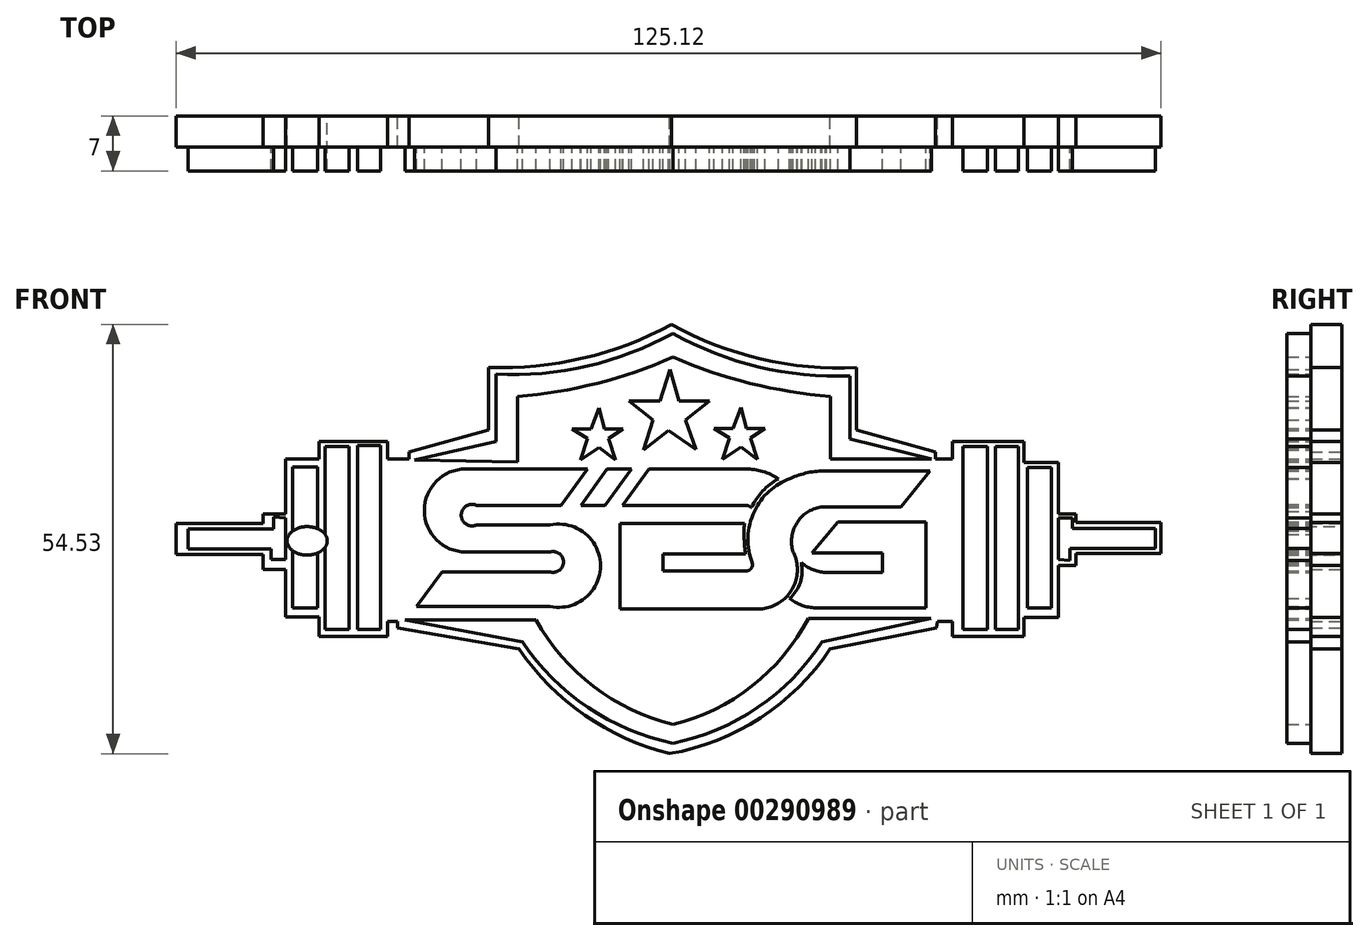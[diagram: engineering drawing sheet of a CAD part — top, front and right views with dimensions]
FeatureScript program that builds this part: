
annotation { "Feature Type Name" : "Feature", "Feature Type Description" : "" }
export const myFeature = defineFeature(function(context is Context, id is Id, definition is map)
    precondition{}
    {
        {
            var Q0;
            Q0=qCreatedBy(makeId("Front.planeOp"),FACE);
            var sketch = newSketch(context, id + "F0", { "sketchPlane" : qUnion([Q0])});
            skLineSegment(sketch, "E0", {"start": v(-28.73, 27.46) * mm, "end": v(-18.36, 29.84) * mm});
            skLineSegment(sketch, "E1", {"start": v(-18.36, 29.84) * mm, "end": v(-18.36, 38.37) * mm});
            skLineSegment(sketch, "E2", {"start": v(26.58, 38.16) * mm, "end": v(26.58, 30.16) * mm});
            skLineSegment(sketch, "E3", {"start": v(26.58, 30.16) * mm, "end": v(36.96, 27.57) * mm});
            skLineSegment(sketch, "E4", {"start": v(36.96, 27.57) * mm, "end": v(24.1, 27.57) * mm});
            skLineSegment(sketch, "E5", {"start": v(24.1, 27.57) * mm, "end": v(24.1, 35.56) * mm});
            skLineSegment(sketch, "E6", {"start": v(-15.66, 35.56) * mm, "end": v(-15.66, 27.24) * mm});
            skLineSegment(sketch, "E7", {"start": v(-15.66, 27.24) * mm, "end": v(-28.73, 27.46) * mm});
            skArc(sketch, "E8", {"start": v(-18.36, 38.37) * mm, "mid": v(-6.76, 39.4) * mm, "end": v(4.11, 43.56) * mm});
            skArc(sketch, "E9", {"start": v(4.11, 43.56) * mm, "mid": v(14.97, 39.29) * mm, "end": v(26.58, 38.16) * mm});
            skArc(sketch, "E10", {"start": v(-15.66, 35.56) * mm, "mid": v(-5.56, 37.2) * mm, "end": v(4.11, 40.53) * mm});
            skArc(sketch, "E11", {"start": v(4.11, 40.53) * mm, "mid": v(13.9, 37.21) * mm, "end": v(24.1, 35.56) * mm});
            skLineSegment(sketch, "E12", {"start": v(-29.92, 7.15) * mm, "end": v(-13.28, 7.15) * mm});
            skLineSegment(sketch, "E13", {"start": v(21.29, 7.37) * mm, "end": v(36.85, 7.37) * mm});
            skLineSegment(sketch, "E14", {"start": v(36.85, 7.37) * mm, "end": v(23.02, 4.34) * mm});
            skLineSegment(sketch, "E15", {"start": v(-15.01, 4.34) * mm, "end": v(-29.92, 7.15) * mm});
            skArc(sketch, "E16", {"start": v(-13.28, 7.15) * mm, "mid": v(-5.98, -1.32) * mm, "end": v(4.11, -6.14) * mm});
            skArc(sketch, "E17", {"start": v(4.11, -6.14) * mm, "mid": v(14.17, -1.26) * mm, "end": v(21.29, 7.37) * mm});
            skArc(sketch, "E18", {"start": v(4.11, -8.52) * mm, "mid": v(14.86, -4) * mm, "end": v(23.02, 4.34) * mm});
            skArc(sketch, "E19", {"start": v(-15.01, 4.34) * mm, "mid": v(-6.71, -3.97) * mm, "end": v(4.11, -8.52) * mm});
            skLineSegment(sketch, "E20.bottom", {"start": v(-35.97, 29.3) * mm, "end": v(-33.05, 29.3) * mm});
            skLineSegment(sketch, "E20.top", {"start": v(-35.97, 5.96) * mm, "end": v(-33.05, 5.96) * mm});
            skLineSegment(sketch, "E20.left", {"start": v(-35.97, 29.3) * mm, "end": v(-35.97, 5.96) * mm});
            skLineSegment(sketch, "E20.right", {"start": v(-33.05, 29.3) * mm, "end": v(-33.05, 5.96) * mm});
            skLineSegment(sketch, "E21.bottom", {"start": v(-40.08, 29.19) * mm, "end": v(-37.05, 29.19) * mm});
            skLineSegment(sketch, "E21.top", {"start": v(-40.08, 5.96) * mm, "end": v(-37.05, 5.96) * mm});
            skLineSegment(sketch, "E21.left", {"start": v(-40.08, 29.19) * mm, "end": v(-40.08, 5.96) * mm});
            skLineSegment(sketch, "E21.right", {"start": v(-37.05, 29.19) * mm, "end": v(-37.05, 5.96) * mm});
            skLineSegment(sketch, "E22.bottom", {"start": v(-44.18, 26.6) * mm, "end": v(-41.05, 26.6) * mm});
            skLineSegment(sketch, "E22.top", {"start": v(-44.18, 8.66) * mm, "end": v(-41.05, 8.66) * mm});
            skLineSegment(sketch, "E22.left", {"start": v(-44.18, 26.6) * mm, "end": v(-44.18, 8.66) * mm});
            skLineSegment(sketch, "E22.right", {"start": v(-41.05, 26.6) * mm, "end": v(-41.05, 8.66) * mm});
            skLineSegment(sketch, "E23.bottom", {"start": v(40.95, 29.19) * mm, "end": v(44.09, 29.19) * mm});
            skLineSegment(sketch, "E23.top", {"start": v(40.95, 5.96) * mm, "end": v(44.09, 5.96) * mm});
            skLineSegment(sketch, "E23.left", {"start": v(40.95, 29.19) * mm, "end": v(40.95, 5.96) * mm});
            skLineSegment(sketch, "E23.right", {"start": v(44.09, 29.19) * mm, "end": v(44.09, 5.96) * mm});
            skLineSegment(sketch, "E24.bottom", {"start": v(45.06, 29.19) * mm, "end": v(47.98, 29.19) * mm});
            skLineSegment(sketch, "E24.top", {"start": v(45.06, 5.96) * mm, "end": v(47.98, 5.96) * mm});
            skLineSegment(sketch, "E24.left", {"start": v(45.06, 29.19) * mm, "end": v(45.06, 5.96) * mm});
            skLineSegment(sketch, "E24.right", {"start": v(47.98, 29.19) * mm, "end": v(47.98, 5.96) * mm});
            skLineSegment(sketch, "E25.bottom", {"start": v(49.16, 26.49) * mm, "end": v(52.19, 26.49) * mm});
            skLineSegment(sketch, "E25.top", {"start": v(49.16, 8.66) * mm, "end": v(52.19, 8.66) * mm});
            skLineSegment(sketch, "E25.left", {"start": v(49.16, 26.49) * mm, "end": v(49.16, 8.66) * mm});
            skLineSegment(sketch, "E25.right", {"start": v(52.19, 26.49) * mm, "end": v(52.19, 8.66) * mm});
            skLineSegment(sketch, "E26", {"start": v(-45.11, 20.09) * mm, "end": v(-45.11, 14.82) * mm});
            skLineSegment(sketch, "E27", {"start": v(-45.11, 14.82) * mm, "end": v(-46.94, 14.82) * mm});
            skLineSegment(sketch, "E28", {"start": v(-46.94, 14.82) * mm, "end": v(-46.94, 16.2) * mm});
            skLineSegment(sketch, "E29", {"start": v(-46.94, 16.2) * mm, "end": v(-57.46, 16.2) * mm});
            skLineSegment(sketch, "E30", {"start": v(-57.46, 16.2) * mm, "end": v(-57.46, 18.72) * mm});
            skLineSegment(sketch, "E31", {"start": v(-57.46, 18.72) * mm, "end": v(-46.6, 18.72) * mm});
            skLineSegment(sketch, "E32", {"start": v(-46.6, 18.72) * mm, "end": v(-46.6, 20.2) * mm});
            skLineSegment(sketch, "E33", {"start": v(-46.6, 20.2) * mm, "end": v(-45.11, 20.09) * mm});
            skLineSegment(sketch, "E34", {"start": v(53.04, 14.85) * mm, "end": v(53.04, 20.12) * mm});
            skLineSegment(sketch, "E35", {"start": v(53.04, 20.12) * mm, "end": v(54.87, 20.12) * mm});
            skLineSegment(sketch, "E36", {"start": v(54.87, 20.12) * mm, "end": v(54.87, 18.74) * mm});
            skLineSegment(sketch, "E37", {"start": v(54.87, 18.74) * mm, "end": v(65.39, 18.74) * mm});
            skLineSegment(sketch, "E38", {"start": v(65.39, 18.74) * mm, "end": v(65.39, 16.22) * mm});
            skLineSegment(sketch, "E39", {"start": v(65.39, 16.22) * mm, "end": v(54.53, 16.22) * mm});
            skLineSegment(sketch, "E40", {"start": v(54.53, 16.22) * mm, "end": v(54.53, 14.74) * mm});
            skLineSegment(sketch, "E41", {"start": v(54.53, 14.74) * mm, "end": v(53.04, 14.85) * mm});
            skLineSegment(sketch, "E42", {"start": v(-8.71, 31.4) * mm, "end": v(-6.3, 31.4) * mm});
            skPoint(sketch, "E42.startSnap0", {"position": v(-15.66, 31.4) * mm});
            skLineSegment(sketch, "E43", {"start": v(-6.3, 31.4) * mm, "end": v(-5.28, 34.1) * mm});
            skLineSegment(sketch, "E44", {"start": v(-5.28, 34.1) * mm, "end": v(-4.56, 31.4) * mm});
            skLineSegment(sketch, "E45", {"start": v(-4.56, 31.4) * mm, "end": v(-2.22, 31.4) * mm});
            skLineSegment(sketch, "E46", {"start": v(-2.22, 31.4) * mm, "end": v(-4.06, 30.22) * mm});
            skLineSegment(sketch, "E47", {"start": v(-4.06, 30.22) * mm, "end": v(-3.2, 27.48) * mm});
            skLineSegment(sketch, "E48", {"start": v(-3.2, 27.48) * mm, "end": v(-5.28, 29.07) * mm});
            skLineSegment(sketch, "E49", {"start": v(-5.28, 29.07) * mm, "end": v(-7.63, 27.48) * mm});
            skLineSegment(sketch, "E50", {"start": v(-7.63, 27.48) * mm, "end": v(-6.76, 30.22) * mm});
            skLineSegment(sketch, "E51", {"start": v(-6.76, 30.22) * mm, "end": v(-8.71, 31.4) * mm});
            skLineSegment(sketch, "E52", {"start": v(3.55, 31.2) * mm, "end": v(0.34, 28.75) * mm});
            skLineSegment(sketch, "E53", {"start": v(0.34, 28.75) * mm, "end": v(1.57, 32.53) * mm});
            skLineSegment(sketch, "E54", {"start": v(1.57, 32.53) * mm, "end": v(-1.5, 34.99) * mm});
            skLineSegment(sketch, "E55", {"start": v(-1.5, 34.99) * mm, "end": v(2.47, 34.99) * mm});
            skLineSegment(sketch, "E56", {"start": v(2.47, 34.99) * mm, "end": v(3.75, 38.94) * mm});
            skLineSegment(sketch, "E57", {"start": v(3.75, 38.94) * mm, "end": v(4.85, 34.99) * mm});
            skLineSegment(sketch, "E58", {"start": v(4.85, 34.99) * mm, "end": v(8.75, 34.99) * mm});
            skLineSegment(sketch, "E59", {"start": v(8.75, 34.99) * mm, "end": v(5.72, 32.53) * mm});
            skLineSegment(sketch, "E60", {"start": v(5.72, 32.53) * mm, "end": v(7.02, 28.78) * mm});
            skLineSegment(sketch, "E61", {"start": v(7.02, 28.78) * mm, "end": v(3.55, 31.2) * mm});
            skLineSegment(sketch, "E62", {"start": v(9.32, 31.47) * mm, "end": v(11.72, 31.47) * mm});
            skLineSegment(sketch, "E63", {"start": v(11.72, 31.47) * mm, "end": v(12.75, 34.16) * mm});
            skLineSegment(sketch, "E64", {"start": v(12.75, 34.16) * mm, "end": v(13.46, 31.47) * mm});
            skLineSegment(sketch, "E65", {"start": v(13.46, 31.47) * mm, "end": v(15.8, 31.47) * mm});
            skLineSegment(sketch, "E66", {"start": v(15.8, 31.47) * mm, "end": v(13.97, 30.29) * mm});
            skLineSegment(sketch, "E67", {"start": v(13.97, 30.29) * mm, "end": v(14.83, 27.55) * mm});
            skLineSegment(sketch, "E68", {"start": v(14.83, 27.55) * mm, "end": v(12.75, 29.13) * mm});
            skLineSegment(sketch, "E69", {"start": v(12.75, 29.13) * mm, "end": v(10.4, 27.55) * mm});
            skLineSegment(sketch, "E70", {"start": v(10.4, 27.55) * mm, "end": v(11.27, 30.29) * mm});
            skLineSegment(sketch, "E71", {"start": v(11.27, 30.29) * mm, "end": v(9.32, 31.47) * mm});
            skLineSegment(sketch, "E72", {"start": v(-6.76, 26.33) * mm, "end": v(-22.2, 26.33) * mm});
            skPoint(sketch, "E72.endSnap0", {"position": v(-22.2, 27.35) * mm});
            skArc(sketch, "E73", {"start": v(-22.2, 26.33) * mm, "mid": v(-27.47, 21.05) * mm, "end": v(-22.2, 15.78) * mm});
            skLineSegment(sketch, "E74", {"start": v(-22.2, 15.78) * mm, "end": v(-11.5, 15.78) * mm});
            skLineSegment(sketch, "E75", {"start": v(-11.5, 13.26) * mm, "end": v(-25.22, 13.26) * mm});
            skLineSegment(sketch, "E76", {"start": v(-25.22, 13.26) * mm, "end": v(-28.48, 8.87) * mm});
            skLineSegment(sketch, "E77", {"start": v(-28.48, 8.87) * mm, "end": v(-11.5, 8.87) * mm});
            skLineSegment(sketch, "E78", {"start": v(-11.5, 19.2) * mm, "end": v(-20.87, 19.2) * mm});
            skLineSegment(sketch, "E79", {"start": v(-20.87, 21.72) * mm, "end": v(-10.1, 21.72) * mm});
            skLineSegment(sketch, "E80", {"start": v(-10.1, 21.72) * mm, "end": v(-6.76, 26.33) * mm});
            skArc(sketch, "E81", {"start": v(-20.87, 21.72) * mm, "mid": v(-22.78, 20.46) * mm, "end": v(-20.87, 19.2) * mm});
            skArc(sketch, "E82", {"start": v(-11.5, 13.26) * mm, "mid": v(-9.8, 14.52) * mm, "end": v(-11.5, 15.78) * mm});
            skArc(sketch, "E83", {"start": v(-11.5, 8.87) * mm, "mid": v(-5.1, 14.04) * mm, "end": v(-11.5, 19.2) * mm});
            skLineSegment(sketch, "E84", {"start": v(-4.24, 26.33) * mm, "end": v(-7.59, 21.72) * mm});
            skLineSegment(sketch, "E85", {"start": v(-7.59, 21.72) * mm, "end": v(-4.52, 21.67) * mm});
            skLineSegment(sketch, "E86", {"start": v(-4.52, 21.67) * mm, "end": v(-1.14, 26.33) * mm});
            skLineSegment(sketch, "E87", {"start": v(-1.14, 26.33) * mm, "end": v(-4.24, 26.33) * mm});
            skLineSegment(sketch, "E88", {"start": v(1.04, 26.33) * mm, "end": v(-2.3, 21.72) * mm});
            skLineSegment(sketch, "E89", {"start": v(-2.3, 21.72) * mm, "end": v(13.27, 21.72) * mm});
            skLineSegment(sketch, "E90", {"start": v(13.34, 26.33) * mm, "end": v(1.04, 26.33) * mm});
            skArc(sketch, "E91", {"start": v(17.5, 25.08) * mm, "mid": v(15.5, 26) * mm, "end": v(13.34, 26.33) * mm});
            skArc(sketch, "E92", {"start": v(17.5, 25.08) * mm, "mid": v(15.5, 23.52) * mm, "end": v(14.07, 21.43) * mm});
            skArc(sketch, "E93", {"start": v(14.07, 21.43) * mm, "mid": v(13.7, 21.65) * mm, "end": v(13.27, 21.72) * mm});
            skLineSegment(sketch, "E94", {"start": v(13.2, 19.4) * mm, "end": v(-2.62, 19.42) * mm});
            skLineSegment(sketch, "E95", {"start": v(-2.62, 19.42) * mm, "end": v(-2.62, 8.55) * mm});
            skLineSegment(sketch, "E96", {"start": v(-2.62, 8.55) * mm, "end": v(14.93, 8.55) * mm});
            skArc(sketch, "E97", {"start": v(14.93, 8.55) * mm, "mid": v(18.63, 10.2) * mm, "end": v(19.88, 14.06) * mm});
            skArc(sketch, "E98", {"start": v(19.88, 14.06) * mm, "mid": v(19.71, 14.96) * mm, "end": v(19.37, 15.8) * mm});
            skArc(sketch, "E99", {"start": v(22.88, 21.5) * mm, "mid": v(19.83, 19.45) * mm, "end": v(19.37, 15.8) * mm});
            skArc(sketch, "E100", {"start": v(13.2, 19.4) * mm, "mid": v(13.15, 17.46) * mm, "end": v(13.34, 15.52) * mm});
            skLineSegment(sketch, "E101", {"start": v(13.34, 15.52) * mm, "end": v(2.81, 15.53) * mm});
            skLineSegment(sketch, "E102", {"start": v(2.81, 15.53) * mm, "end": v(2.81, 13.36) * mm});
            skLineSegment(sketch, "E103", {"start": v(2.81, 13.36) * mm, "end": v(13.34, 13.35) * mm});
            skArc(sketch, "E104", {"start": v(13.34, 13.35) * mm, "mid": v(13.98, 13.62) * mm, "end": v(14.24, 14.27) * mm});
            skArc(sketch, "E105", {"start": v(14.47, 20.95) * mm, "mid": v(13.63, 17.64) * mm, "end": v(14.24, 14.27) * mm});
            skArc(sketch, "E106", {"start": v(19, 25.1) * mm, "mid": v(16.3, 23.5) * mm, "end": v(14.47, 20.95) * mm});
            skArc(sketch, "E107", {"start": v(23.6, 26.09) * mm, "mid": v(21.25, 25.86) * mm, "end": v(19, 25.1) * mm});
            skLineSegment(sketch, "E108", {"start": v(23.6, 26.09) * mm, "end": v(36.74, 26.09) * mm});
            skLineSegment(sketch, "E109", {"start": v(36.74, 26.09) * mm, "end": v(33.05, 21.53) * mm});
            skLineSegment(sketch, "E110", {"start": v(33.05, 21.53) * mm, "end": v(22.88, 21.5) * mm});
            skArc(sketch, "E111", {"start": v(18.92, 9.85) * mm, "mid": v(20.3, 11.94) * mm, "end": v(20.4, 14.44) * mm});
            skArc(sketch, "E112", {"start": v(18.92, 9.85) * mm, "mid": v(20.48, 9.02) * mm, "end": v(22.22, 8.67) * mm});
            skArc(sketch, "E113", {"start": v(20.4, 14.44) * mm, "mid": v(21.83, 13.56) * mm, "end": v(23.46, 13.17) * mm});
            skLineSegment(sketch, "E114", {"start": v(23.46, 13.17) * mm, "end": v(30.7, 13.17) * mm});
            skLineSegment(sketch, "E115", {"start": v(30.7, 13.17) * mm, "end": v(30.7, 15.64) * mm});
            skLineSegment(sketch, "E116", {"start": v(30.7, 15.64) * mm, "end": v(21.79, 15.64) * mm});
            skLineSegment(sketch, "E117", {"start": v(21.79, 15.64) * mm, "end": v(25.08, 19.6) * mm});
            skLineSegment(sketch, "E118", {"start": v(25.08, 19.6) * mm, "end": v(36.27, 19.6) * mm});
            skLineSegment(sketch, "E119", {"start": v(36.27, 19.6) * mm, "end": v(36.27, 8.67) * mm});
            skLineSegment(sketch, "E120", {"start": v(36.27, 8.67) * mm, "end": v(22.22, 8.67) * mm});
            skSolve(sketch);
        }
        {
            var Q0;
            Q0=qCreatedBy(makeId("Front.planeOp"),FACE);
            var sketch = newSketch(context, id + "F1", { "sketchPlane" : qUnion([Q0])});
            skLineSegment(sketch, "E121", {"start": v(-59.01, 15.48) * mm, "end": v(-47.98, 15.48) * mm});
            skLineSegment(sketch, "E122", {"start": v(-47.98, 15.48) * mm, "end": v(-47.98, 13.54) * mm});
            skLineSegment(sketch, "E123", {"start": v(-47.98, 13.54) * mm, "end": v(-45.1, 13.54) * mm});
            skLineSegment(sketch, "E124", {"start": v(-45.1, 13.54) * mm, "end": v(-45.1, 7.56) * mm});
            skLineSegment(sketch, "E125", {"start": v(-45.1, 7.56) * mm, "end": v(-40.84, 7.56) * mm});
            skLineSegment(sketch, "E126", {"start": v(-40.84, 7.56) * mm, "end": v(-40.84, 5.07) * mm});
            skLineSegment(sketch, "E127", {"start": v(-40.84, 5.07) * mm, "end": v(-32.14, 5.07) * mm});
            skLineSegment(sketch, "E128", {"start": v(-32.14, 5.07) * mm, "end": v(-32.14, 6.93) * mm});
            skLineSegment(sketch, "E129", {"start": v(-32.14, 6.93) * mm, "end": v(-30.9, 6.93) * mm});
            skLineSegment(sketch, "E130", {"start": v(-30.9, 6.93) * mm, "end": v(-30.9, 6.16) * mm});
            skLineSegment(sketch, "E131", {"start": v(-30.9, 6.16) * mm, "end": v(-15.44, 3.44) * mm});
            skArc(sketch, "E132", {"start": v(-15.44, 3.44) * mm, "mid": v(-7.1, -4.95) * mm, "end": v(3.69, -9.84) * mm});
            skArc(sketch, "E133", {"start": v(3.69, -9.84) * mm, "mid": v(15.24, -5.29) * mm, "end": v(24.07, 3.44) * mm});
            skLineSegment(sketch, "E134", {"start": v(24.07, 3.44) * mm, "end": v(37.57, 6.16) * mm});
            skLineSegment(sketch, "E135", {"start": v(37.57, 6.16) * mm, "end": v(37.7, 6.93) * mm});
            skLineSegment(sketch, "E136", {"start": v(37.7, 6.93) * mm, "end": v(39.64, 6.93) * mm});
            skLineSegment(sketch, "E137", {"start": v(39.64, 6.93) * mm, "end": v(39.64, 5.07) * mm});
            skLineSegment(sketch, "E138", {"start": v(39.64, 5.07) * mm, "end": v(48.67, 5.07) * mm});
            skLineSegment(sketch, "E139", {"start": v(48.67, 5.07) * mm, "end": v(48.67, 7.47) * mm});
            skLineSegment(sketch, "E140", {"start": v(48.67, 7.47) * mm, "end": v(53.09, 7.47) * mm});
            skLineSegment(sketch, "E141", {"start": v(53.09, 7.47) * mm, "end": v(53.09, 14.07) * mm});
            skLineSegment(sketch, "E142", {"start": v(53.09, 14.07) * mm, "end": v(55.3, 14.07) * mm});
            skLineSegment(sketch, "E143", {"start": v(55.3, 14.07) * mm, "end": v(55.3, 15.57) * mm});
            skLineSegment(sketch, "E144", {"start": v(55.3, 15.57) * mm, "end": v(66.1, 15.57) * mm});
            skLineSegment(sketch, "E145", {"start": v(66.1, 15.57) * mm, "end": v(66.1, 19.5) * mm});
            skLineSegment(sketch, "E146", {"start": v(66.1, 19.5) * mm, "end": v(55.3, 19.5) * mm});
            skLineSegment(sketch, "E147", {"start": v(55.3, 19.5) * mm, "end": v(55.3, 20.64) * mm});
            skLineSegment(sketch, "E148", {"start": v(55.3, 20.64) * mm, "end": v(53.09, 20.64) * mm});
            skLineSegment(sketch, "E149", {"start": v(53.09, 20.64) * mm, "end": v(53.09, 27.12) * mm});
            skLineSegment(sketch, "E150", {"start": v(53.09, 27.12) * mm, "end": v(48.67, 27.12) * mm});
            skLineSegment(sketch, "E151", {"start": v(48.67, 27.12) * mm, "end": v(48.67, 29.82) * mm});
            skLineSegment(sketch, "E152", {"start": v(48.67, 29.82) * mm, "end": v(39.62, 29.82) * mm});
            skLineSegment(sketch, "E153", {"start": v(39.62, 29.82) * mm, "end": v(39.62, 27.58) * mm});
            skLineSegment(sketch, "E154", {"start": v(39.62, 27.58) * mm, "end": v(37.44, 27.58) * mm});
            skLineSegment(sketch, "E155", {"start": v(37.44, 27.58) * mm, "end": v(37.44, 28.46) * mm});
            skLineSegment(sketch, "E156", {"start": v(37.44, 28.46) * mm, "end": v(27.43, 31.26) * mm});
            skLineSegment(sketch, "E157", {"start": v(27.43, 31.26) * mm, "end": v(27.43, 39.23) * mm});
            skArc(sketch, "E158", {"start": v(3.92, 44.7) * mm, "mid": v(15.29, 40.3) * mm, "end": v(27.43, 39.23) * mm});
            skArc(sketch, "E159", {"start": v(-19.3, 39.23) * mm, "mid": v(-7.32, 40.4) * mm, "end": v(3.92, 44.7) * mm});
            skLineSegment(sketch, "E160", {"start": v(-19.3, 39.23) * mm, "end": v(-19.3, 31.26) * mm});
            skLineSegment(sketch, "E161", {"start": v(-19.3, 31.26) * mm, "end": v(-29.4, 28.46) * mm});
            skLineSegment(sketch, "E162", {"start": v(-29.4, 28.46) * mm, "end": v(-29.4, 27.58) * mm});
            skLineSegment(sketch, "E163", {"start": v(-29.4, 27.58) * mm, "end": v(-32.14, 27.58) * mm});
            skLineSegment(sketch, "E164", {"start": v(-32.14, 27.58) * mm, "end": v(-32.14, 29.82) * mm});
            skLineSegment(sketch, "E165", {"start": v(-32.14, 29.82) * mm, "end": v(-40.84, 29.82) * mm});
            skLineSegment(sketch, "E166", {"start": v(-40.84, 29.82) * mm, "end": v(-40.84, 27.58) * mm});
            skLineSegment(sketch, "E167", {"start": v(-40.84, 27.58) * mm, "end": v(-45.1, 27.58) * mm});
            skLineSegment(sketch, "E168", {"start": v(-45.1, 27.58) * mm, "end": v(-45.1, 20.64) * mm});
            skLineSegment(sketch, "E169", {"start": v(-45.1, 20.64) * mm, "end": v(-47.98, 20.64) * mm});
            skLineSegment(sketch, "E170", {"start": v(-47.98, 20.64) * mm, "end": v(-47.98, 19.4) * mm});
            skLineSegment(sketch, "E171", {"start": v(-47.98, 19.4) * mm, "end": v(-59.01, 19.4) * mm});
            skLineSegment(sketch, "E172", {"start": v(-59.01, 19.4) * mm, "end": v(-59.01, 15.48) * mm});
            skPoint(sketch, "E173.centerSnap0", {"position": v(-7.1, -4.95) * mm});
            skPoint(sketch, "E173.center.orphan", {"position": v(3.69, -4.95) * mm});
            skPoint(sketch, "E174.center.orphan", {"position": v(3.69, -2.04) * mm});
            skEllipse(sketch, "E175", {"center": v(-42.36, 17.2) * mm, "majorRadius": 2.56 * mm, "minorRadius": 1.8 * mm, "majorAxis": v(1, 0)});
            skSolve(sketch);
        }
        {
            var Q0;
            Q0=qSketchRegion(id+"F1",true);
            extrude(context, id + "F2", {"entities" : qUnion([Q0]), "depth" : 4 * mm});
        }
        {
            var Q0;
            Q0=qSketchRegion(id+"F0",true);
            extrude(context, id + "F3", {"entities" : qUnion([Q0]), "operationType" : NewBodyOperationType.ADD, "depth" : 7 * mm});
        }
        {
            var Q0;
            Q0=makeQuery(id+"F1.imprint","IMPRINT",FACE,{"disambiguationData":[TD([[makeQuery(id+"F1.imprint","IMPRINT",EDGE,{"derivedFrom":sQuery(id+"F1.wireOp",EDGE,"E175")}),1.0]])]});
            var Q1;
            Q1=sQuery(id+"F1.wireOp",EDGE,"E175");
            extrude(context, id + "F4", {"entities" : qUnion([Q0]), "operationType" : NewBodyOperationType.REMOVE, "surfaceEntities" : qUnion([Q1]), "endBound" : BoundingType.THROUGH_ALL, "depth" : 25 * mm});
        }
    });
